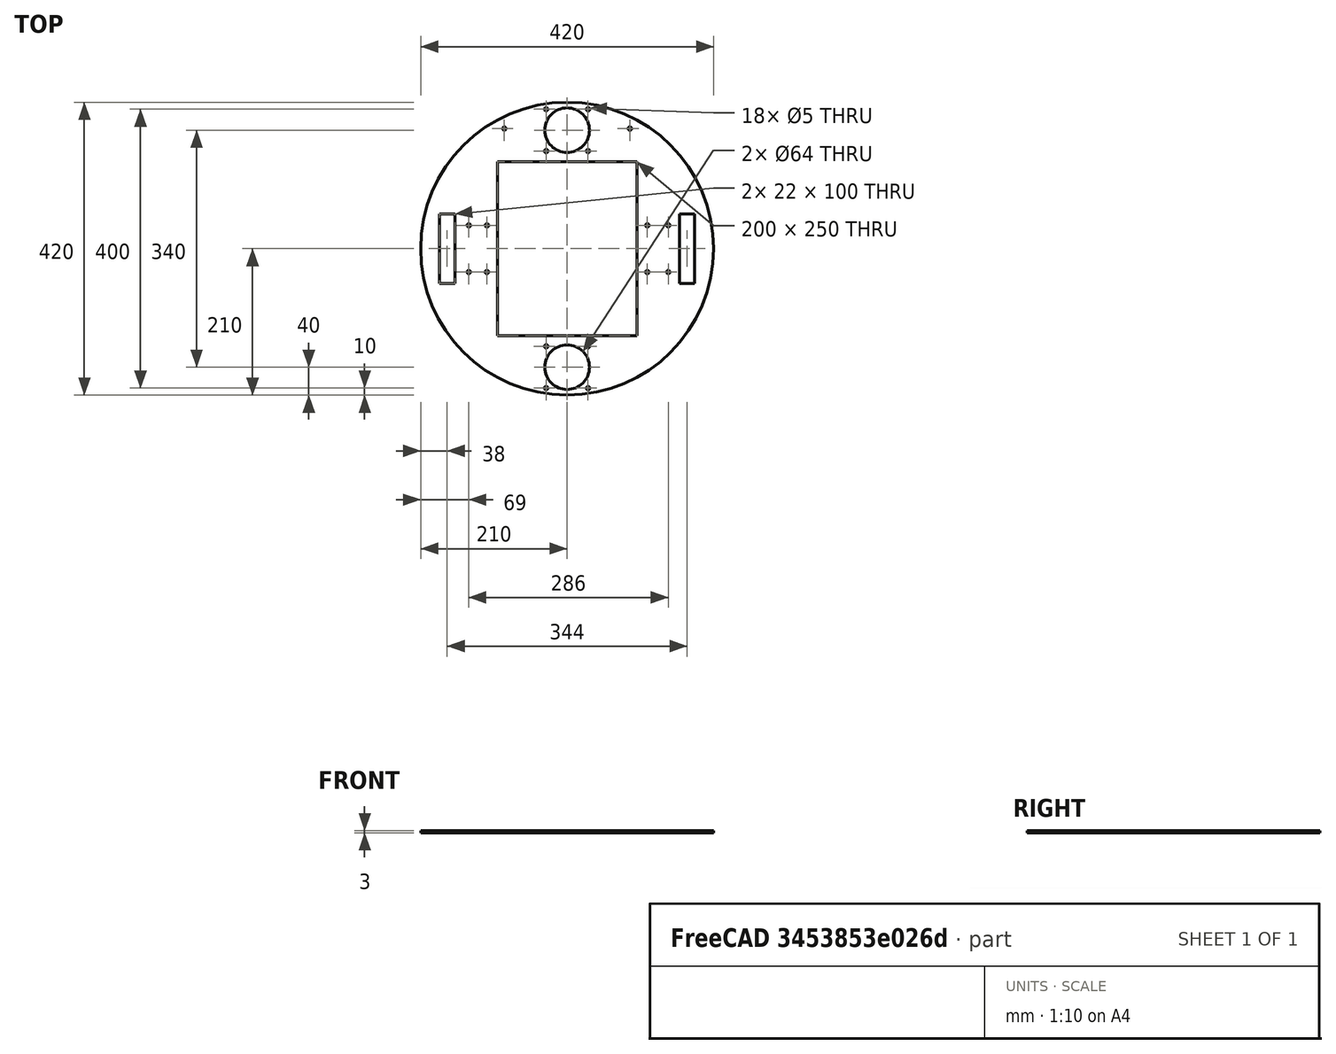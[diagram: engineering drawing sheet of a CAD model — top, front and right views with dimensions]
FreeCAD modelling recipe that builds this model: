
FCSTD DOCUMENT  (FreeCAD 0.15R4671 (Git))
Label: base
License: All rights reserved
LicenseURL: http://en.wikipedia.org/wiki/All_rights_reserved
objects: Drawing::FeatureViewPart×3, Sketcher::SketchObject×1, PartDesign::Pad×1, Drawing::FeaturePage×1
note: 3 computed .brp shape members not serialized (recipe doc carries the construction recipe); baked Part::Feature solids carry a one-line shape summary decoded from their .brp

FEATURE [Sketcher::SketchObject] Sketch
  sketch-geometry (33):
    g0: Circle CenterX=0 CenterY=0 CenterZ=0 NormalX=0 NormalY=0 NormalZ=1 Radius=210
    g1: Circle CenterX=0 CenterY=170 CenterZ=0 NormalX=0 NormalY=0 NormalZ=1 Radius=32
    g2: Circle CenterX=0 CenterY=-170 CenterZ=0 NormalX=0 NormalY=0 NormalZ=1 Radius=32
    g3: Circle CenterX=-141 CenterY=33.5 CenterZ=0 NormalX=0 NormalY=0 NormalZ=1 Radius=2.5
    g4: Circle CenterX=-141 CenterY=-33.5 CenterZ=0 NormalX=0 NormalY=0 NormalZ=1 Radius=2.5
    g5: Circle CenterX=-115 CenterY=33.5 CenterZ=0 NormalX=0 NormalY=0 NormalZ=1 Radius=2.5
    g6: Circle CenterX=-115 CenterY=-33.5 CenterZ=0 NormalX=0 NormalY=0 NormalZ=1 Radius=2.5
    g7: LineSegment StartX=-161 StartY=-50 StartZ=0 EndX=-183 EndY=-50 EndZ=0
    g8: LineSegment StartX=-183 StartY=-50 StartZ=0 EndX=-183 EndY=50 EndZ=0
    g9: LineSegment StartX=-183 StartY=50 StartZ=0 EndX=-161 EndY=50 EndZ=0
    g10: LineSegment StartX=-161 StartY=50 StartZ=0 EndX=-161 EndY=-50 EndZ=0
    g11: Circle CenterX=115 CenterY=33.5 CenterZ=0 NormalX=0 NormalY=0 NormalZ=1 Radius=2.5
    g12: Circle CenterX=115 CenterY=-33.5 CenterZ=0 NormalX=0 NormalY=0 NormalZ=1 Radius=2.5
    g13: Circle CenterX=145 CenterY=33.5 CenterZ=0 NormalX=0 NormalY=0 NormalZ=1 Radius=2.5
    g14: Circle CenterX=145 CenterY=-33.5 CenterZ=0 NormalX=0 NormalY=0 NormalZ=1 Radius=2.5
    g15: LineSegment StartX=183 StartY=50 StartZ=0 EndX=161 EndY=50 EndZ=0
    g16: LineSegment StartX=161 StartY=50 StartZ=0 EndX=161 EndY=-50 EndZ=0
    g17: LineSegment StartX=161 StartY=-50 StartZ=0 EndX=183 EndY=-50 EndZ=0
    g18: LineSegment StartX=183 StartY=-50 StartZ=0 EndX=183 EndY=50 EndZ=0
    g19: Circle CenterX=-90 CenterY=172.291 CenterZ=0 NormalX=0 NormalY=0 NormalZ=1 Radius=2.5
    g20: Circle CenterX=90 CenterY=172.291 CenterZ=0 NormalX=0 NormalY=0 NormalZ=1 Radius=2.5
    g21: Circle CenterX=-30 CenterY=200 CenterZ=0 NormalX=0 NormalY=0 NormalZ=1 Radius=2.5
    g22: Circle CenterX=30 CenterY=200 CenterZ=0 NormalX=0 NormalY=0 NormalZ=1 Radius=2.5
    g23: Circle CenterX=-30 CenterY=140 CenterZ=0 NormalX=0 NormalY=0 NormalZ=1 Radius=2.5
    g24: Circle CenterX=30 CenterY=140 CenterZ=0 NormalX=0 NormalY=0 NormalZ=1 Radius=2.5
    g25: Circle CenterX=-30 CenterY=-140 CenterZ=0 NormalX=0 NormalY=0 NormalZ=1 Radius=2.5
    g26: Circle CenterX=30 CenterY=-140 CenterZ=0 NormalX=0 NormalY=0 NormalZ=1 Radius=2.5
    g27: Circle CenterX=-30 CenterY=-200 CenterZ=0 NormalX=0 NormalY=0 NormalZ=1 Radius=2.5
    g28: Circle CenterX=30 CenterY=-200 CenterZ=0 NormalX=0 NormalY=0 NormalZ=1 Radius=2.5
    g29: LineSegment StartX=-100 StartY=125 StartZ=0 EndX=100 EndY=125 EndZ=0
    g30: LineSegment StartX=100 StartY=125 StartZ=0 EndX=100 EndY=-125 EndZ=0
    g31: LineSegment StartX=100 StartY=-125 StartZ=0 EndX=-100 EndY=-125 EndZ=0
    g32: LineSegment StartX=-100 StartY=-125 StartZ=0 EndX=-100 EndY=125 EndZ=0
  constraints (75):
    c: Coincident(g0,g-1)
    c: Radius(g0) = 210
    c: PointOnObject(g1,g-2)
    c: PointOnObject(g2,g-2)
    c: Equal(g2,g1)
    c: Equal(g4,g3)
    c: Symmetric(g3,g4,g-1)
    c: Equal(g5,g3)
    c: Equal(g6,g5)
    c: Coincident(g7,g8)
    c: Coincident(g8,g9)
    c: Coincident(g9,g10)
    c: Coincident(g10,g7)
    c: Horizontal(g7)
    c: Horizontal(g9)
    c: Vertical(g8)
    c: Vertical(g10)
    c: Equal(g5,g11)
    c: Equal(g13,g12)
    c: Equal(g12,g14)
    c: Equal(g14,g11)
    c: Coincident(g15,g16)
    c: Coincident(g16,g17)
    c: Coincident(g17,g18)
    c: Coincident(g18,g15)
    c: Horizontal(g15)
    c: Horizontal(g17)
    c: Vertical(g16)
    c: Vertical(g18)
    c: Symmetric(g11,g5,g-2)
    c: Symmetric(g12,g6,g-2)
    c: Symmetric(g14,g13,g-1)
    c: Equal(g10,g16)
    c: Equal(g15,g9)
    c: Symmetric(g15,g9,g-2)
    c: Symmetric(g20,g19,g-2)
    c: DistanceX(g-1,g19) = -90
    c: Radius(g21) = 2.5
    c: Symmetric(g21,g22,g-2)
    c: DistanceX(g-1,g21) = -30
    c: Equal(g21,g22)
    c: Symmetric(g24,g23,g-2)
    c: Equal(g28,g26)
    c: Equal(g26,g25)
    c: Equal(g25,g27)
    c: Equal(g27,g21)
    c: Symmetric(g27,g28,g-2)
    c: Symmetric(g26,g25,g-2)
    c: Symmetric(g23,g25,g-1)
    c: Symmetric(g21,g27,g-1)
    c: Equal(g19,g21)
    c: Equal(g20,g21)
    c: DistanceY(g8) = 100
    c: DistanceX(g7) = -22
    c: DistanceY(g23,g21) = 60
    c: DistanceX(g23,g24) = 60
    c: Symmetric(g9,g7,g-1)
    c: DistanceX(g3,g9) = -20
    c: DistanceY(g-1,g1) = 170
    c: Symmetric(g2,g1,g-1)
    c: DistanceY(g22,g1) = -30
    c: Coincident(g29,g30)
    c: Coincident(g30,g31)
    c: Coincident(g31,g32)
    c: Coincident(g32,g29)
    c: Horizontal(g29)
    c: Horizontal(g31)
    c: Vertical(g30)
    c: Vertical(g32)
    c: DistanceY(g32) = 250
    c: DistanceX(g31) = -200
    c: Symmetric(g31,g30,g-2)
    c: Symmetric(g29,g31,g-1)
    c: Radius(g2) = 32
    c: DistanceX(g-1,g7) = -161
FEATURE [PartDesign::Pad] Pad
  Length = 3
  Length2 = 100
  Midplane = true
  Sketch = -> Sketch
  Type = 0
FEATURE [Drawing::FeatureViewPart] Ortho  label="Ortho_0_0"
  Direction = (1,0,0)
  HiddenWidth = 0.15
  LineWidth = 0.35
  Rotation = -90
  Scale = 0.25
  ShowHiddenLines = false
  ShowSmoothLines = false
  Source = -> Pad
  Tolerance = 0.05
  ViewResult = <g id="Ortho_0_0"\n   transform="rotate(-90,91.5,147.542) translate(91.5,147.542) scale(0.25,0.25)"\n  >\n<g   stroke="rgb(0, 0, 0)"\n   stroke-width="1.4"\n   stroke-linecap="butt"\n   stroke-linejoin="miter"\n   fill="none"\n   transform="scale(1,-1)"\n  >\n<path id= "1" d=" M 1.5 210 L -1.5 210 " />\n<path id= "2" d=" M 1.5 -210 L -1.5 -210 " />\n</g>\n<g   stroke="rgb(0, 0, 0)"\n   stroke-width="1.4"\n   stroke-linecap="butt"\n   stroke-linejoin="miter"\n   fill="none"\n   transform="scale(1,-1)"\n  >\n<path d="M-1.5,0 L-1.5,-23.5125  L-1.5,-46.7294  L-1.5,-69.3586  L-1.5,-91.1156  L-1.5,-111.727  L-1.5,-130.933  L-1.5,-148.492  L-1.5,-164.185  L-1.5,-177.812  L-1.5,-189.203  L-1.5,-198.215  L-1.5,-204.735  L-1.5,-208.68  L-1.5,-210 " /><path d="M-1.5,210 L-1.5,208.68  L-1.5,204.735  L-1.5,198.215  L-1.5,189.203  L-1.5,177.812  L-1.5,164.185  L-1.5,148.492  L-1.5,130.933  L-1.5,111.727  L-1.5,91.1156  L-1.5,69.3586  L-1.5,46.7294  L-1.5,23.5125  L-1.5,-6.94635e-13 " /><path d="M1.5,0 L1.5,-23.5125  L1.5,-46.7294  L1.5,-69.3586  L1.5,-91.1156  L1.5,-111.727  L1.5,-130.933  L1.5,-148.492  L1.5,-164.185  L1.5,-177.812  L1.5,-189.203  L1.5,-198.215  L1.5,-204.735  L1.5,-208.68  L1.5,-210 " /><path d="M1.5,210 L1.5,208.68  L1.5,204.735  L1.5,198.215  L1.5,189.203  L1.5,177.812  L1.5,164.185  L1.5,148.492  L1.5,130.933  L1.5,111.727  L1.5,91.1156  L1.5,69.3586  L1.5,46.7294  L1.5,23.5125  L1.5,-6.94635e-13 " /></g>\n</g>
  Visible = true
  X = 91.5
  Y = 147.542
FEATURE [Drawing::FeatureViewPart] Ortho002  label="Ortho_1_1"
  Direction = (0.57735,0.57735,0.57735)
  HiddenWidth = 0.15
  LineWidth = 0.35
  Rotation = 120
  Scale = 0.25
  ShowHiddenLines = false
  ShowSmoothLines = false
  Source = -> Pad
  Tolerance = 0.05
  ViewResult = <blob: 7607 chars omitted>
  Visible = true
  X = 215.5
  Y = 78.5833
FEATURE [Drawing::FeatureViewPart] Ortho003  label="Ortho_0_1"
  Direction = (0,0,1)
  HiddenWidth = 0.15
  LineWidth = 0.35
  Rotation = 90
  Scale = 0.25
  ShowHiddenLines = false
  ShowSmoothLines = false
  Source = -> Pad
  Tolerance = 0.05
  ViewResult = <g id="Ortho_0_1"\n   transform="rotate(90,91.5,78.5833) translate(91.5,78.5833) scale(0.25,0.25)"\n  >\n<g   stroke="rgb(0, 0, 0)"\n   stroke-width="1.4"\n   stroke-linecap="butt"\n   stroke-linejoin="miter"\n   fill="none"\n   transform="scale(1,-1)"\n  >\n<circle cx ="0" cy ="0" r ="210" /><path id= "2" d=" M -100 125 L 100 125 " />\n<path id= "3" d=" M 100 125 L 100 -125 " />\n<path id= "4" d=" M 100 -125 L -100 -125 " />\n<path id= "5" d=" M -100 -125 L -100 125 " />\n<path id= "6" d=" M -161 -50 L -183 -50 " />\n<path id= "7" d=" M -183 -50 L -183 50 " />\n<path id= "8" d=" M -183 50 L -161 50 " />\n<path id= "9" d=" M -161 50 L -161 -50 " />\n<path id= "10" d=" M 183 50 L 161 50 " />\n<path id= "11" d=" M 161 50 L 161 -50 " />\n<path id= "12" d=" M 161 -50 L 183 -50 " />\n<path id= "13" d=" M 183 -50 L 183 50 " />\n<circle cx ="0" cy ="170" r ="32" /><circle cx ="0" cy ="-170" r ="32" /><circle cx ="90" cy ="172.291" r ="2.5" /><circle cx ="-90" cy ="172.291" r ="2.5" /><circle cx ="-141" cy ="33.5" r ="2.5" /><circle cx ="-141" cy ="-33.5" r ="2.5" /><circle cx ="-115" cy ="33.5" r ="2.5" /><circle cx ="-115" cy ="-33.5" r ="2.5" /><circle cx ="30" cy ="-200" r ="2.5" /><circle cx ="115" cy ="33.5" r ="2.5" /><circle cx ="115" cy ="-33.5" r ="2.5" /><circle cx ="145" cy ="-33.5" r ="2.5" /><circle cx ="-30" cy ="-200" r ="2.5" /><circle cx ="-30" cy ="200" r ="2.5" /><circle cx ="30" cy ="200" r ="2.5" /><circle cx ="-30" cy ="140" r ="2.5" /><circle cx ="30" cy ="140" r ="2.5" /><circle cx ="-30" cy ="-140" r ="2.5" /><circle cx ="30" cy ="-140" r ="2.5" /><circle cx ="145" cy ="33.5" r ="2.5" /></g>\n</g>
  Visible = true
  X = 91.5
  Y = 78.5833
FEATURE [Drawing::FeaturePage] Page
  EditableTexts = Siqueira | Siqueira | Pindí | Drawing | Base 2 | 0016 | 2015-06-21
  Group = -> [Ortho,Ortho002,Ortho003]
  Template = <path>
note: 1 file-system path scrubbed to <path> (originals preserved in the JSON sidecar)
